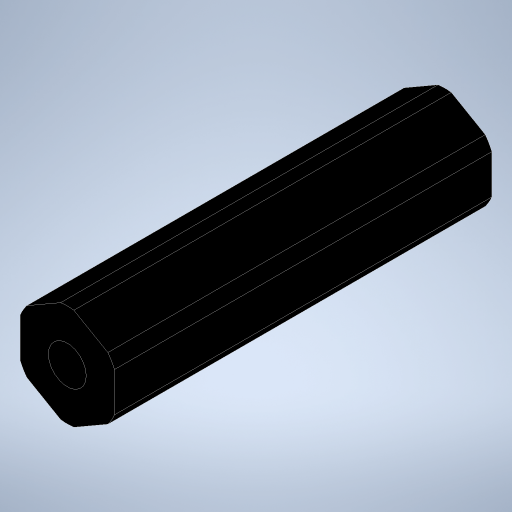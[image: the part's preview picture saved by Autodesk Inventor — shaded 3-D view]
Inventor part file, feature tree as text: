
AUTODESK INVENTOR PART (.ipt)
format: ipt  version: 2023.3 (Build 273359000, 359)  size: 239,104 bytes
history: native  units: in
note: dims shown in document units (in); Inventor stores cm internally (conversion verified against a paired STEP export)
features: sketch x3, extrude x2, projected_geometry x2, hole x1
ambient origin geometry x8: Origin, YZ Plane, XZ Plane, XY Plane, X Axis, Y Axis, Z Axis, Center Point
bodies: Solid1 (feature_tree)
feature tree (8):
  extrude  "Extrusion1"  Depth=1.0in
  hole  "Hole1"  [1 undecoded]
  extrude  "Extrusion3"  [1 undecoded]
  sketch  "Sketch1"  dims[d2=0.0in]
  sketch  "Sketch3"  dims[d9=0.625in d10=0.385in d11=0.25in d12=0.5635in d13=1.0in d14=0.8108in d16=0.7in]
  sketch  "Sketch4"  dims[d17=0.0in d18=0.0in]
  projected_geometry  "Project Cut Edges1"
  projected_geometry  "Project Cut Edges2"
note: 2 required parameter values undecoded (feature->parameter linkage not recoverable at this tier; creation-order binding heuristic only, values carry confidence <= 0.55)
